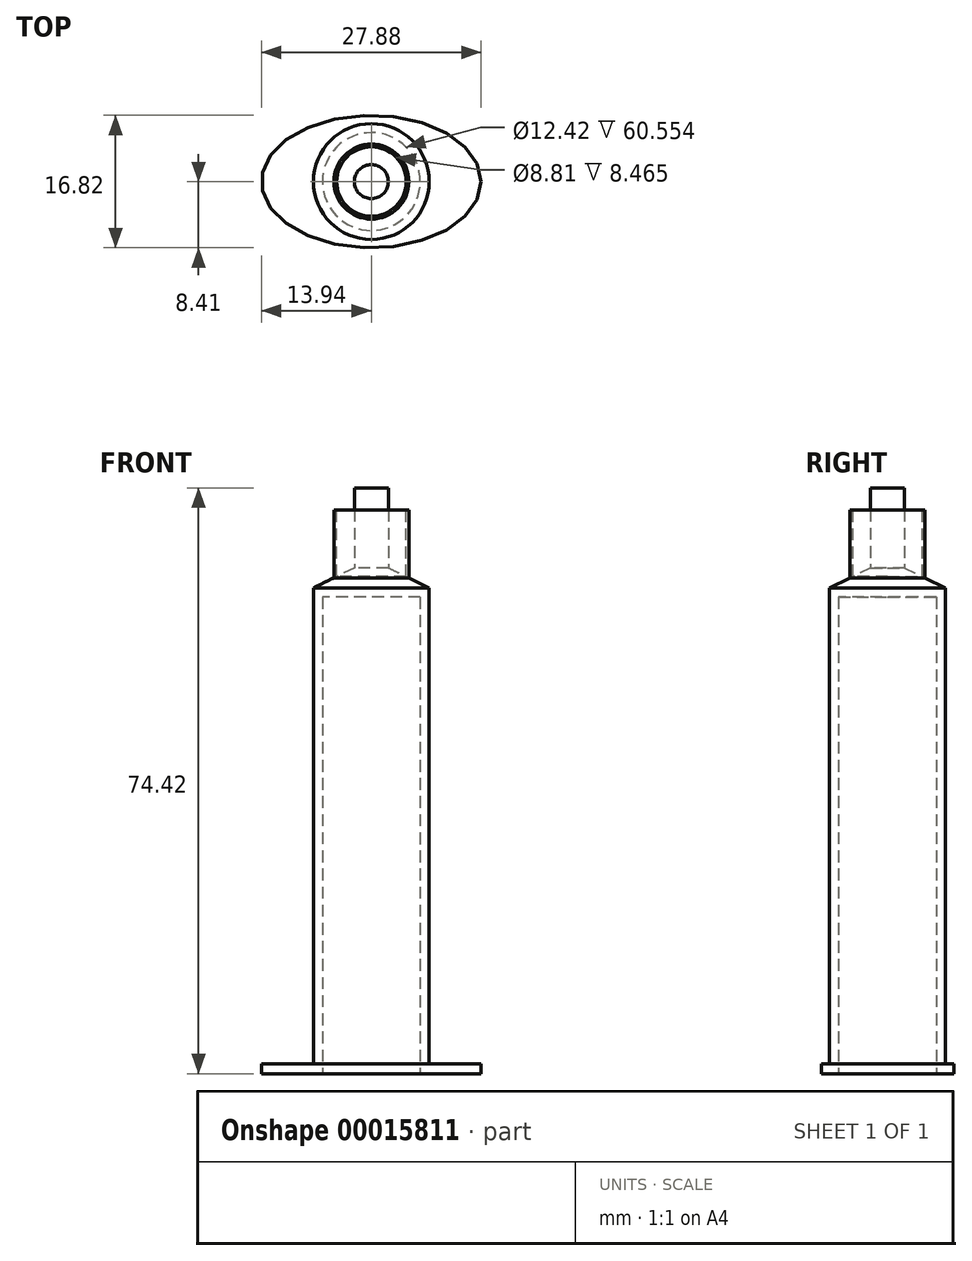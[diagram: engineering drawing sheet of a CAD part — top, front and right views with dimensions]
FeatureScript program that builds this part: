
annotation { "Feature Type Name" : "Feature", "Feature Type Description" : "" }
export const myFeature = defineFeature(function(context is Context, id is Id, definition is map)
    precondition{}
    {
        {
            var Q0;
            Q0=qCreatedBy(makeId("Top.planeOp"),FACE);
            var sketch = newSketch(context, id + "F0", { "sketchPlane" : qUnion([Q0])});
            skCircle(sketch, "E0", {"center": v(0, 0) * mm, "radius": 7.35 * mm});
            skCircle(sketch, "E1", {"center": v(0, 0) * mm, "radius": 6.21 * mm});
            skSolve(sketch);
        }
        {
            var Q0;
            Q0 = qSketchRegion(id + "F0", true);
            extrude(context, id + "F1", {"entities" : qUnion([Q0]), "depth" : 59.28 * mm});
        }
        {
            var Q0;
            Q0=makeQuery(id+"F1.opExtrude","CAP_FACE",FACE,{"disambiguationData":[OSD([sQuery(id+"F0.wireOp",EDGE,"E0"),sQuery(id+"F0.wireOp",EDGE,"E1")])],"isStart":true});
            var sketch = newSketch(context, id + "F2", { "sketchPlane" : qUnion([Q0])});
            skEllipse(sketch, "E2", {"center": v(0, 0) * mm, "majorRadius": 13.94 * mm, "minorRadius": 8.4 * mm, "majorAxis": v(1, 0)});
            skSolve(sketch);
        }
        {
            var Q0;
            Q0=makeQuery(id+"F2.imprint","IMPRINT",FACE,{"disambiguationData":[TD([[makeQuery(id+"F2.imprint","IMPRINT",EDGE,{"derivedFrom":sQuery(id+"F2.wireOp",EDGE,"E2")}),1.0]])]});
            var Q1;
            Q1=makeQuery(id+"F2.imprint","IMPRINT",FACE,{"disambiguationData":[TD([[makeQuery(id+"F2.imprint","IMPRINT",EDGE,{"derivedFrom":makeQuery(id+"F1.opExtrude","CAP_EDGE",EDGE,{"disambiguationData":[OSD([sQuery(id+"F0.wireOp",EDGE,"E0")])],"isStart":true})}),-1.0]])]});
            extrude(context, id + "F3", {"entities" : qUnion([Q0, Q1]), "operationType" : NewBodyOperationType.ADD, "depth" : 1.27 * mm});
        }
        {
            var Q0;
            Q0=makeQuery(id+"F1.opExtrude","CAP_FACE",FACE,{"disambiguationData":[OSD([sQuery(id+"F0.wireOp",EDGE,"E0"),sQuery(id+"F0.wireOp",EDGE,"E1")])],"isStart":false});
            var sketch = newSketch(context, id + "F4", { "sketchPlane" : qUnion([Q0])});
            skCircle(sketch, "E3", {"center": v(0, 0) * mm, "radius": 7.35 * mm});
            skSolve(sketch);
        }
        {
            var Q0;
            Q0 = qSketchRegion(id + "F4", true);
            extrude(context, id + "F5", {"entities" : qUnion([Q0]), "operationType" : NewBodyOperationType.ADD, "depth" : 3.7 * mm});
        }
        {
            var Q0;
            Q0=makeQuery(id+"F5.opExtrude","CAP_FACE",FACE,{"disambiguationData":[OSD([sQuery(id+"F4.wireOp",EDGE,"E3")])],"isStart":false});
            var sketch = newSketch(context, id + "F6", { "sketchPlane" : qUnion([Q0])});
            skCircle(sketch, "E4", {"center": v(0, 0) * mm, "radius": 2.16 * mm});
            skSolve(sketch);
        }
        {
            var Q0;
            Q0 = qSketchRegion(id + "F6", true);
            extrude(context, id + "F7", {"entities" : qUnion([Q0]), "operationType" : NewBodyOperationType.ADD, "depth" : 10.16 * mm});
        }
        {
            var Q0;
            Q0=makeQuery(id+"F5.opExtrude","CAP_EDGE",EDGE,{"disambiguationData":[OSD([sQuery(id+"F4.wireOp",EDGE,"E3")])],"isStart":false});
            chamfer(context, id + "F8", {"entities" : qUnion([Q0]), "chamferType" : ChamferType.TWO_OFFSETS, "width1" : 5.2 * mm, "oppositeDirection" : false, "width2" : 2.54 * mm, "tangentPropagation" : true});
        }
        {
            var Q0;
            Q0=makeQuery(id+"F7.opExtrude","CAP_FACE",FACE,{"disambiguationData":[OSD([sQuery(id+"F6.wireOp",EDGE,"E4")])],"isStart":false});
            cPlane(context, id + "F9", {"entities" : qUnion([Q0]), "cplaneType" : CPlaneType.OFFSET, "offset" : 2.8 * mm, "oppositeDirection" : true, "width" : 152.4 * mm, "height" : 152.4 * mm});
        }
        {
            var Q0;
            Q0=qCreatedBy(id+"F9.planeOp",FACE);
            var sketch = newSketch(context, id + "F10", { "sketchPlane" : qUnion([Q0])});
            skCircle(sketch, "E5", {"center": v(0, 0) * mm, "radius": 4.76 * mm});
            skCircle(sketch, "E6", {"center": v(0, 0) * mm, "radius": 4.4 * mm});
            skSolve(sketch);
        }
        {
            var Q0;
            Q0 = qSketchRegion(id + "F10", true);
            var Q1;
            Q1=makeQuery(id+"F8.opChamfer","BLEND_FACE",FACE,{"disambiguationData":[OSD([sQuery(id+"F4.wireOp",EDGE,"E3")])]});
            extrude(context, id + "F11", {"entities" : qUnion([Q0]), "operationType" : NewBodyOperationType.ADD, "endBound" : BoundingType.UP_TO_SURFACE, "oppositeDirection" : true, "endBoundEntityFace" : qUnion([Q1]), "depth" : 25.4 * mm});
        }
    });
